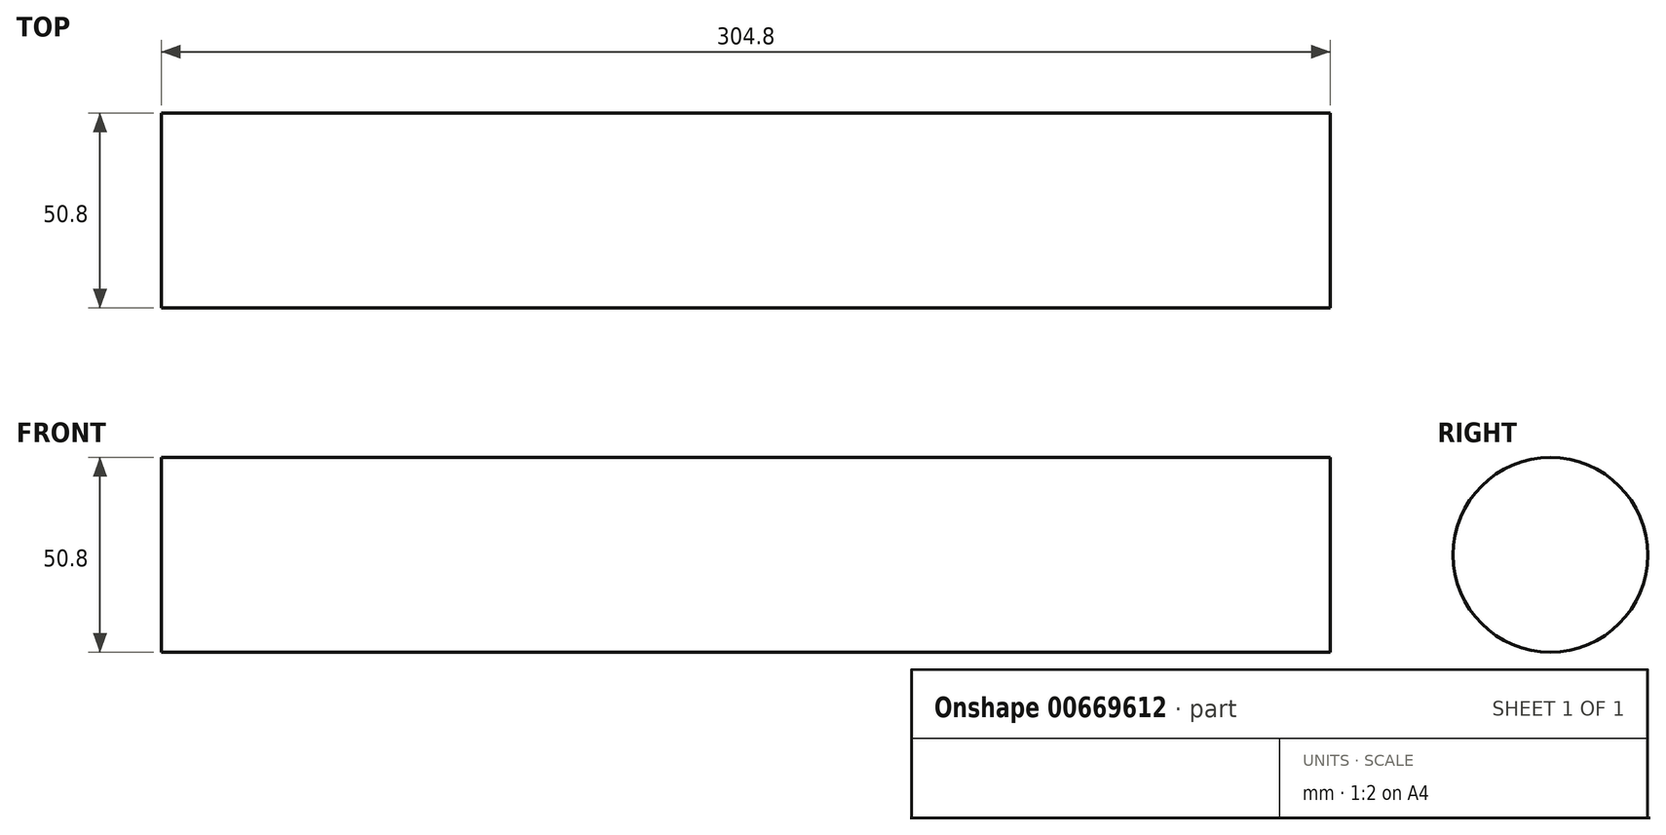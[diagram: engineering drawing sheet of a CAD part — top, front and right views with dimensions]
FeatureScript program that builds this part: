
annotation { "Feature Type Name" : "Feature", "Feature Type Description" : "" }
export const myFeature = defineFeature(function(context is Context, id is Id, definition is map)
    precondition{}
    {
        {
            var Q0;
            Q0=qCreatedBy(makeId("Front.planeOp"),FACE);
            var sketch = newSketch(context, id + "F0", { "sketchPlane" : qUnion([Q0])});
            skLineSegment(sketch, "E0.bottom", {"start": v(0, 0) * mm, "end": v(304.8, 0) * mm});
            skLineSegment(sketch, "E0.top", {"start": v(0, 25.4) * mm, "end": v(304.8, 25.4) * mm});
            skLineSegment(sketch, "E0.left", {"start": v(0, 0) * mm, "end": v(0, 25.4) * mm});
            skLineSegment(sketch, "E0.right", {"start": v(304.8, 0) * mm, "end": v(304.8, 25.4) * mm});
            skSolve(sketch);
        }
        {
            var Q0;
            Q0=makeQuery(id+"F0.imprint","IMPRINT",FACE,{"disambiguationData":[TD([[makeQuery(id+"F0.imprint","IMPRINT",EDGE,{"derivedFrom":sQuery(id+"F0.wireOp",EDGE,"E0.bottom")}),1.0]])]});
            var Q1;
            Q1=sQuery(id+"F0.wireOp",EDGE,"E0.bottom");
            revolve(context, id + "F1", {"entities" : qUnion([Q0]), "axis" : qUnion([Q1]), "revolveType" : RevolveType.FULL});
        }
    });
